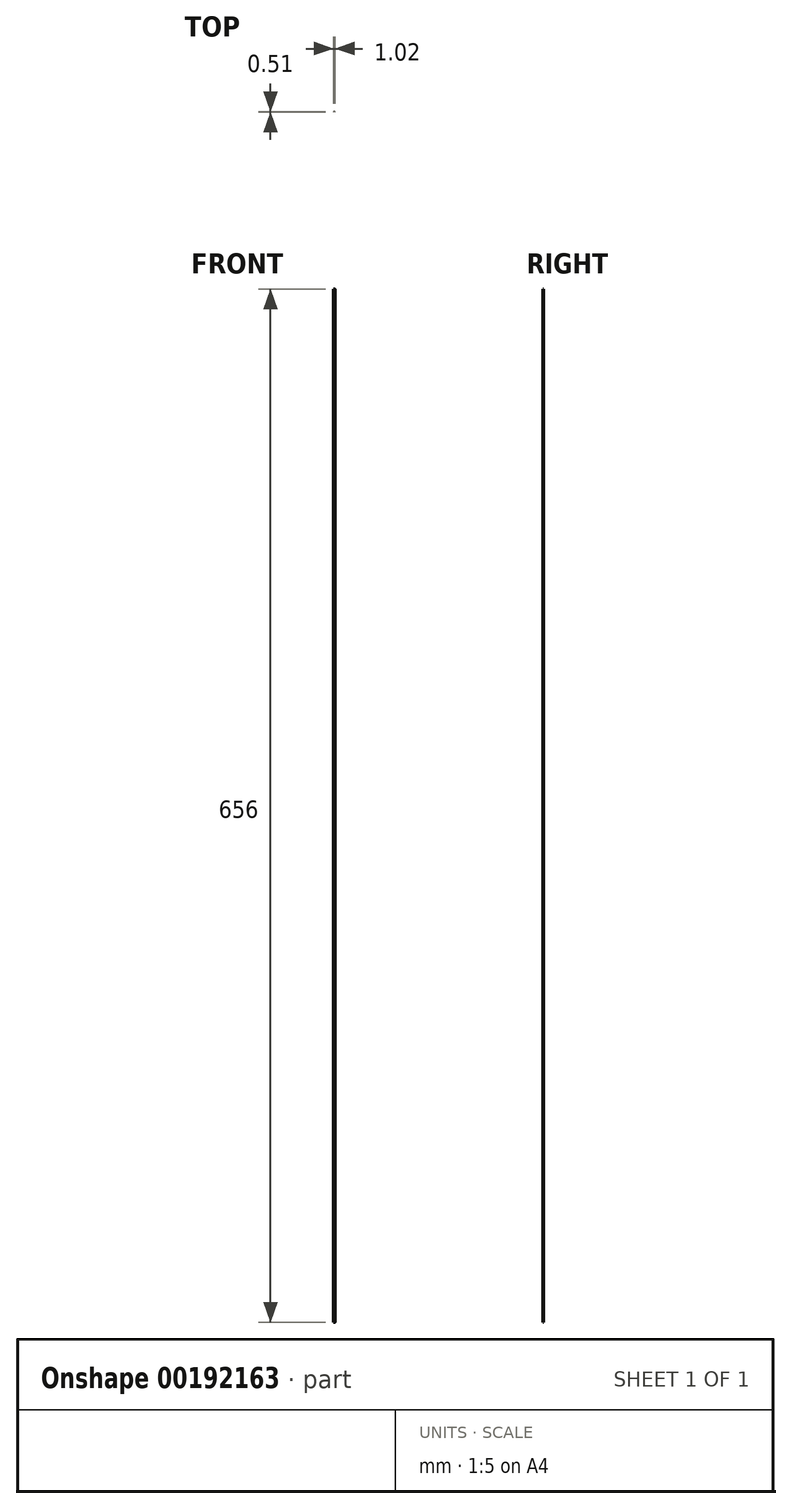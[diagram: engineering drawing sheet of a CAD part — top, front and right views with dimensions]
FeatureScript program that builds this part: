
annotation { "Feature Type Name" : "Feature", "Feature Type Description" : "" }
export const myFeature = defineFeature(function(context is Context, id is Id, definition is map)
    precondition{}
    {
        {
            var Q0;
            Q0=qCreatedBy(makeId("Top.planeOp"),FACE);
            var sketch = newSketch(context, id + "F0", { "sketchPlane" : qUnion([Q0])});
            skLineSegment(sketch, "E0.0", {"start": v(-3.9, 22.38) * mm, "end": v(-0.61, 19.1) * mm});
            skPoint(sketch, "E1.0", {"position": v(-5.03, 22.6) * mm});
            skArc(sketch, "E2.0", {"start": v(-5.66, 21.65) * mm, "mid": v(-5.03, 22.6) * mm, "end": v(-3.9, 22.38) * mm});
            skLineSegment(sketch, "E3.0", {"start": v(-5.66, 19.54) * mm, "end": v(-5.66, 21.65) * mm});
            skArc(sketch, "E4.0", {"start": v(-6.7, 18.5) * mm, "mid": v(-5.97, 18.8) * mm, "end": v(-5.66, 19.54) * mm});
            skArc(sketch, "E5.0.0", {"start": v(0.88, 9.83) * mm, "mid": v(1.9, 10.51) * mm, "end": v(3.12, 10.76) * mm});
            skLineSegment(sketch, "E5.0.1", {"start": v(3.12, 10.76) * mm, "end": v(6.54, 10.76) * mm});
            skArc(sketch, "E5.0.2", {"start": v(6.54, 10.76) * mm, "mid": v(7.75, 10.51) * mm, "end": v(8.78, 9.83) * mm});
            skLineSegment(sketch, "E5.0.3", {"start": v(8.78, 9.83) * mm, "end": v(12, 6.6) * mm});
            skArc(sketch, "E5.0.4", {"start": v(12, 6.6) * mm, "mid": v(12.24, 5.43) * mm, "end": v(11.25, 4.76) * mm});
            skLineSegment(sketch, "E5.0.5", {"start": v(11.25, 4.76) * mm, "end": v(9.12, 4.76) * mm});
            skArc(sketch, "E5.0.6", {"start": v(9.12, 4.76) * mm, "mid": v(8.38, 4.45) * mm, "end": v(8.07, 3.71) * mm});
            skLineSegment(sketch, "E5.0.7", {"start": v(8.07, 3.71) * mm, "end": v(8.07, 3.6) * mm});
            skArc(sketch, "E5.0.8", {"start": v(8.07, 3.6) * mm, "mid": v(8.38, 2.86) * mm, "end": v(9.12, 2.55) * mm});
            skLineSegment(sketch, "E5.0.9", {"start": v(9.12, 2.55) * mm, "end": v(10.15, 2.55) * mm});
            skArc(sketch, "E5.0.10", {"start": v(10.15, 2.55) * mm, "mid": v(10.66, 3.06) * mm, "end": v(11.16, 2.55) * mm});
            skLineSegment(sketch, "E5.0.11", {"start": v(11.16, 2.55) * mm, "end": v(14.38, 2.55) * mm});
            skArc(sketch, "E5.0.12", {"start": v(14.38, 2.55) * mm, "mid": v(14.89, 3.06) * mm, "end": v(15.4, 2.55) * mm});
            skArc(sketch, "E5.0.13", {"start": v(15.4, 2.55) * mm, "mid": v(16.91, 3.17) * mm, "end": v(17.53, 4.69) * mm});
            skArc(sketch, "E5.0.14", {"start": v(17.53, 4.69) * mm, "mid": v(17.02, 5.2) * mm, "end": v(17.53, 5.7) * mm});
            skLineSegment(sketch, "E5.0.15", {"start": v(17.53, 5.7) * mm, "end": v(17.53, 8.92) * mm});
            skArc(sketch, "E5.0.16", {"start": v(17.53, 8.92) * mm, "mid": v(17.02, 9.43) * mm, "end": v(17.53, 9.93) * mm});
            skLineSegment(sketch, "E5.0.17", {"start": v(17.53, 9.93) * mm, "end": v(17.53, 10.96) * mm});
            skArc(sketch, "E5.0.18", {"start": v(17.53, 10.96) * mm, "mid": v(17.22, 11.7) * mm, "end": v(16.48, 12.01) * mm});
            skLineSegment(sketch, "E5.0.19", {"start": v(16.48, 12.01) * mm, "end": v(16.37, 12.01) * mm});
            skArc(sketch, "E5.0.20", {"start": v(16.37, 12.01) * mm, "mid": v(15.63, 11.7) * mm, "end": v(15.32, 10.96) * mm});
            skLineSegment(sketch, "E5.0.21", {"start": v(15.32, 10.96) * mm, "end": v(15.32, 8.85) * mm});
            skArc(sketch, "E5.0.22", {"start": v(15.32, 8.85) * mm, "mid": v(14.69, 7.9) * mm, "end": v(13.57, 8.12) * mm});
            skLineSegment(sketch, "E5.0.23", {"start": v(13.57, 8.12) * mm, "end": v(10.27, 11.41) * mm});
            skArc(sketch, "E5.0.24", {"start": v(10.27, 11.41) * mm, "mid": v(9.58, 12.44) * mm, "end": v(9.34, 13.66) * mm});
            skLineSegment(sketch, "E5.0.25", {"start": v(9.34, 13.66) * mm, "end": v(9.34, 16.85) * mm});
            skArc(sketch, "E5.0.26", {"start": v(9.34, 16.85) * mm, "mid": v(9.58, 18.06) * mm, "end": v(10.27, 19.1) * mm});
            skLineSegment(sketch, "E5.0.27", {"start": v(10.27, 19.1) * mm, "end": v(13.57, 22.38) * mm});
            skArc(sketch, "E5.0.28", {"start": v(13.57, 22.38) * mm, "mid": v(14.69, 22.6) * mm, "end": v(15.32, 21.65) * mm});
            skLineSegment(sketch, "E5.0.29", {"start": v(15.32, 21.65) * mm, "end": v(15.32, 19.54) * mm});
            skArc(sketch, "E5.0.30", {"start": v(15.32, 19.54) * mm, "mid": v(15.63, 18.8) * mm, "end": v(16.37, 18.5) * mm});
            skLineSegment(sketch, "E5.0.31", {"start": v(16.37, 18.5) * mm, "end": v(16.48, 18.5) * mm});
            skArc(sketch, "E5.0.32", {"start": v(16.48, 18.5) * mm, "mid": v(17.22, 18.8) * mm, "end": v(17.53, 19.54) * mm});
            skLineSegment(sketch, "E5.0.33", {"start": v(17.53, 19.54) * mm, "end": v(17.53, 20.57) * mm});
            skArc(sketch, "E5.0.34", {"start": v(17.53, 20.57) * mm, "mid": v(17.02, 21.08) * mm, "end": v(17.53, 21.58) * mm});
            skLineSegment(sketch, "E5.0.35", {"start": v(17.53, 21.58) * mm, "end": v(17.53, 24.8) * mm});
            skArc(sketch, "E5.0.36", {"start": v(17.53, 24.8) * mm, "mid": v(17.02, 25.31) * mm, "end": v(17.53, 25.82) * mm});
            skArc(sketch, "E5.0.37", {"start": v(17.53, 25.82) * mm, "mid": v(16.91, 27.33) * mm, "end": v(15.4, 27.95) * mm});
            skArc(sketch, "E5.0.38", {"start": v(15.4, 27.95) * mm, "mid": v(14.89, 27.44) * mm, "end": v(14.38, 27.95) * mm});
            skLineSegment(sketch, "E5.0.39", {"start": v(14.38, 27.95) * mm, "end": v(11.16, 27.95) * mm});
            skArc(sketch, "E5.0.40", {"start": v(11.16, 27.95) * mm, "mid": v(10.66, 27.44) * mm, "end": v(10.15, 27.95) * mm});
            skLineSegment(sketch, "E5.0.41", {"start": v(10.15, 27.95) * mm, "end": v(9.12, 27.95) * mm});
            skArc(sketch, "E5.0.42", {"start": v(9.12, 27.95) * mm, "mid": v(8.38, 27.64) * mm, "end": v(8.07, 26.9) * mm});
            skLineSegment(sketch, "E5.0.43", {"start": v(8.07, 26.9) * mm, "end": v(8.07, 26.8) * mm});
            skArc(sketch, "E5.0.44", {"start": v(8.07, 26.8) * mm, "mid": v(8.38, 26.05) * mm, "end": v(9.12, 25.74) * mm});
            skLineSegment(sketch, "E5.0.45", {"start": v(9.12, 25.74) * mm, "end": v(11.3, 25.74) * mm});
            skArc(sketch, "E5.0.46", {"start": v(11.3, 25.74) * mm, "mid": v(12.26, 25.1) * mm, "end": v(12.04, 23.98) * mm});
            skLineSegment(sketch, "E5.0.47", {"start": v(12.04, 23.98) * mm, "end": v(8.73, 20.68) * mm});
            skArc(sketch, "E5.0.48", {"start": v(8.73, 20.68) * mm, "mid": v(7.7, 19.99) * mm, "end": v(6.49, 19.75) * mm});
            skLineSegment(sketch, "E5.0.49", {"start": v(6.49, 19.75) * mm, "end": v(3.17, 19.75) * mm});
            skArc(sketch, "E5.0.50", {"start": v(3.17, 19.75) * mm, "mid": v(1.96, 19.99) * mm, "end": v(0.93, 20.68) * mm});
            skLineSegment(sketch, "E5.0.51", {"start": v(0.93, 20.68) * mm, "end": v(-2.38, 23.98) * mm});
            skArc(sketch, "E5.0.52", {"start": v(-2.38, 23.98) * mm, "mid": v(-2.6, 25.1) * mm, "end": v(-1.65, 25.74) * mm});
            skLineSegment(sketch, "E5.0.53", {"start": v(-1.65, 25.74) * mm, "end": v(0.54, 25.74) * mm});
            skArc(sketch, "E5.0.54", {"start": v(0.54, 25.74) * mm, "mid": v(1.28, 26.05) * mm, "end": v(1.6, 26.8) * mm});
            skLineSegment(sketch, "E5.0.55", {"start": v(1.6, 26.8) * mm, "end": v(1.6, 26.9) * mm});
            skArc(sketch, "E5.0.56", {"start": v(1.6, 26.9) * mm, "mid": v(1.28, 27.64) * mm, "end": v(0.54, 27.95) * mm});
            skLineSegment(sketch, "E5.0.57", {"start": v(0.54, 27.95) * mm, "end": v(-0.49, 27.95) * mm});
            skArc(sketch, "E5.0.58", {"start": v(-0.49, 27.95) * mm, "mid": v(-1, 27.44) * mm, "end": v(-1.5, 27.95) * mm});
            skLineSegment(sketch, "E5.0.59", {"start": v(-1.5, 27.95) * mm, "end": v(-4.72, 27.95) * mm});
            skArc(sketch, "E5.0.60", {"start": v(-4.72, 27.95) * mm, "mid": v(-5.23, 27.44) * mm, "end": v(-5.74, 27.95) * mm});
            skArc(sketch, "E5.0.61", {"start": v(-5.74, 27.95) * mm, "mid": v(-7.25, 27.33) * mm, "end": v(-7.87, 25.82) * mm});
            skArc(sketch, "E5.0.62", {"start": v(-7.87, 25.82) * mm, "mid": v(-7.36, 25.31) * mm, "end": v(-7.87, 24.8) * mm});
            skLineSegment(sketch, "E5.0.63", {"start": v(-7.87, 24.8) * mm, "end": v(-7.87, 21.58) * mm});
            skArc(sketch, "E5.0.64", {"start": v(-7.87, 21.58) * mm, "mid": v(-7.36, 21.08) * mm, "end": v(-7.87, 20.57) * mm});
            skLineSegment(sketch, "E5.0.65", {"start": v(-7.87, 20.57) * mm, "end": v(-7.87, 19.54) * mm});
            skArc(sketch, "E5.0.66", {"start": v(-7.87, 19.54) * mm, "mid": v(-7.56, 18.8) * mm, "end": v(-6.82, 18.5) * mm});
            skLineSegment(sketch, "E5.0.67", {"start": v(-6.82, 18.5) * mm, "end": v(-6.7, 18.5) * mm});
            skArc(sketch, "E5.0.72", {"start": v(-0.61, 19.1) * mm, "mid": v(0.08, 18.06) * mm, "end": v(0.32, 16.85) * mm});
            skLineSegment(sketch, "E5.0.73", {"start": v(0.32, 16.85) * mm, "end": v(0.32, 13.66) * mm});
            skArc(sketch, "E5.0.74", {"start": v(0.32, 13.66) * mm, "mid": v(0.08, 12.44) * mm, "end": v(-0.61, 11.41) * mm});
            skLineSegment(sketch, "E5.0.75", {"start": v(-0.61, 11.41) * mm, "end": v(-3.9, 8.12) * mm});
            skArc(sketch, "E5.0.76", {"start": v(-3.9, 8.12) * mm, "mid": v(-5.03, 7.9) * mm, "end": v(-5.66, 8.85) * mm});
            skLineSegment(sketch, "E5.0.77", {"start": v(-5.66, 8.85) * mm, "end": v(-5.66, 10.96) * mm});
            skArc(sketch, "E5.0.78", {"start": v(-5.66, 10.96) * mm, "mid": v(-5.97, 11.7) * mm, "end": v(-6.7, 12.01) * mm});
            skLineSegment(sketch, "E5.0.79", {"start": v(-6.7, 12.01) * mm, "end": v(-6.82, 12.01) * mm});
            skArc(sketch, "E5.0.80", {"start": v(-6.82, 12.01) * mm, "mid": v(-7.56, 11.7) * mm, "end": v(-7.87, 10.96) * mm});
            skLineSegment(sketch, "E5.0.81", {"start": v(-7.87, 10.96) * mm, "end": v(-7.87, 9.93) * mm});
            skArc(sketch, "E5.0.82", {"start": v(-7.87, 9.93) * mm, "mid": v(-7.36, 9.43) * mm, "end": v(-7.87, 8.92) * mm});
            skLineSegment(sketch, "E5.0.83", {"start": v(-7.87, 8.92) * mm, "end": v(-7.87, 5.7) * mm});
            skArc(sketch, "E5.0.84", {"start": v(-7.87, 5.7) * mm, "mid": v(-7.36, 5.2) * mm, "end": v(-7.87, 4.69) * mm});
            skArc(sketch, "E5.0.85", {"start": v(-7.87, 4.69) * mm, "mid": v(-7.25, 3.17) * mm, "end": v(-5.74, 2.55) * mm});
            skArc(sketch, "E5.0.86", {"start": v(-5.74, 2.55) * mm, "mid": v(-5.23, 3.06) * mm, "end": v(-4.72, 2.55) * mm});
            skLineSegment(sketch, "E5.0.87", {"start": v(-4.72, 2.55) * mm, "end": v(-1.5, 2.55) * mm});
            skArc(sketch, "E5.0.88", {"start": v(-1.5, 2.55) * mm, "mid": v(-1, 3.06) * mm, "end": v(-0.49, 2.55) * mm});
            skLineSegment(sketch, "E5.0.89", {"start": v(-0.49, 2.55) * mm, "end": v(0.54, 2.55) * mm});
            skArc(sketch, "E5.0.90", {"start": v(0.54, 2.55) * mm, "mid": v(1.28, 2.86) * mm, "end": v(1.6, 3.6) * mm});
            skLineSegment(sketch, "E5.0.91", {"start": v(1.6, 3.6) * mm, "end": v(1.6, 3.71) * mm});
            skArc(sketch, "E5.0.92", {"start": v(1.6, 3.71) * mm, "mid": v(1.28, 4.45) * mm, "end": v(0.54, 4.76) * mm});
            skLineSegment(sketch, "E5.0.93", {"start": v(0.54, 4.76) * mm, "end": v(-1.59, 4.76) * mm});
            skArc(sketch, "E5.0.94", {"start": v(-1.59, 4.76) * mm, "mid": v(-2.58, 5.43) * mm, "end": v(-2.35, 6.6) * mm});
            skLineSegment(sketch, "E5.0.95", {"start": v(-2.35, 6.6) * mm, "end": v(0.88, 9.83) * mm});
            skSolve(sketch);
        }
        {
            var Q0;
            Q0=makeQuery(id+"F0.imprint","IMPRINT",FACE,{"disambiguationData":[TD([[makeQuery(id+"F0.imprint","IMPRINT",EDGE,{"derivedFrom":sQuery(id+"F0.wireOp",EDGE,"E5.0.12")}),1.0]])]});
            extrude(context, id + "F1", {"entities" : qUnion([Q0]), "depth" : 656 * mm});
        }
    });
